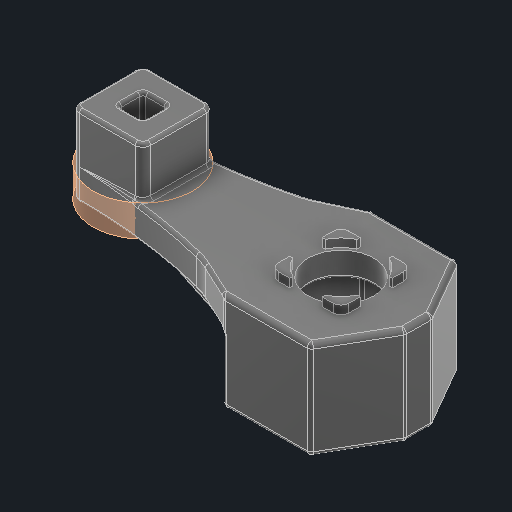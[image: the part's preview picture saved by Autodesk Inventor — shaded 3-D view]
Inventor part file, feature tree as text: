
AUTODESK INVENTOR PART (.ipt)
format: ipt  version: 2025 (Build 290162000, 162)  size: 598,016 bytes
history: native  units: in
note: dims shown in document units (in); Inventor stores cm internally (conversion verified against a paired STEP export)
features: other x5, sketch x2
ambient origin geometry x8: Origin, YZ Plane, XZ Plane, XY Plane, X Axis, Y Axis, Z Axis, Center Point
bodies: Solid1 (feature_tree)
feature tree (7):
  other  "1-Post Standoff Retainer.ipt"
  other  "Solid1::1-Post Standoff Retainer.ipt"
  other  "TaggingFeature1"
  sketch  "Sketch1"  dims[d0=0.3937in]
  sketch  "Sketch2"
  other  "Srf1"
  other  "Srf1::Derived"
